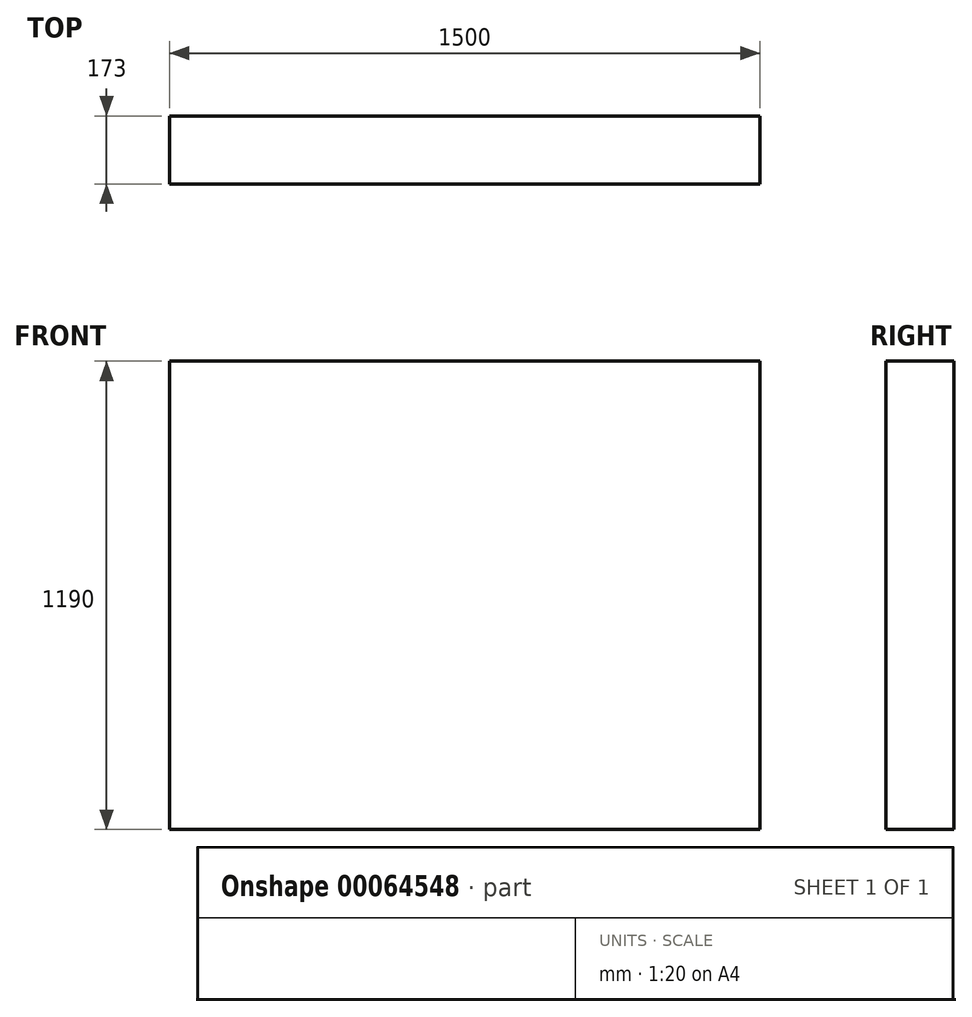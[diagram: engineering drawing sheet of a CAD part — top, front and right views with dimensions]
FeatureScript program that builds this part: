
annotation { "Feature Type Name" : "Feature", "Feature Type Description" : "" }
export const myFeature = defineFeature(function(context is Context, id is Id, definition is map)
    precondition{}
    {
        {
            var Q0;
            Q0=qCreatedBy(makeId("Front.planeOp"),FACE);
            var sketch = newSketch(context, id + "F0", { "sketchPlane" : qUnion([Q0])});
            skLineSegment(sketch, "E0.bottom", {"start": v(-1190, 0) * mm, "end": v(310, 0) * mm});
            skLineSegment(sketch, "E0.top", {"start": v(-1190, 1190) * mm, "end": v(310, 1190) * mm});
            skLineSegment(sketch, "E0.left", {"start": v(-1190, 0) * mm, "end": v(-1190, 1190) * mm});
            skLineSegment(sketch, "E0.right", {"start": v(310, 0) * mm, "end": v(310, 1190) * mm});
            skSolve(sketch);
        }
        {
            var Q0;
            Q0=makeQuery(id+"F0.imprint","IMPRINT",FACE,{"disambiguationData":[TD([[makeQuery(id+"F0.imprint","IMPRINT",EDGE,{"derivedFrom":sQuery(id+"F0.wireOp",EDGE,"E0.bottom")}),1.0]])]});
            extrude(context, id + "F1", {"entities" : qUnion([Q0]), "depth" : 173 * mm});
        }
    });
